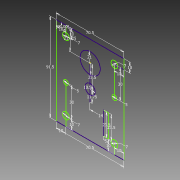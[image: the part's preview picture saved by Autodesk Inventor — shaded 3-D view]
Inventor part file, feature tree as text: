
AUTODESK INVENTOR PART (.ipt)
format: ipt  version: 2015 (Build 190159000, 159)  size: 93,184 bytes
history: native  units: mm
features: sketch x1
ambient origin geometry x8: Origin, YZ Plane, XZ Plane, XY Plane, X Axis, Y Axis, Z Axis, Center Point
feature tree (1):
  sketch  "Sketch1"  dims[d0=21.0mm d1=23.5mm d2=10.5mm d3=11.75mm d5=23.5mm d6=5.0mm d7=23.5mm d9=70.5mm d40=21.625mm d41=70.5mm d42=91.5mm d43=10.0mm d44=10.0mm d45=7.0mm d46=10.0mm d47=10.0mm d48=90.0deg d50=7.0mm d51=10.0mm d52=10.0mm d53=7.0mm d54=10.0mm d55=10.0mm d56=7.0mm d60=30.0mm d61=30.0mm d62=5.0mm d63=5.0mm d64=14.0mm]
